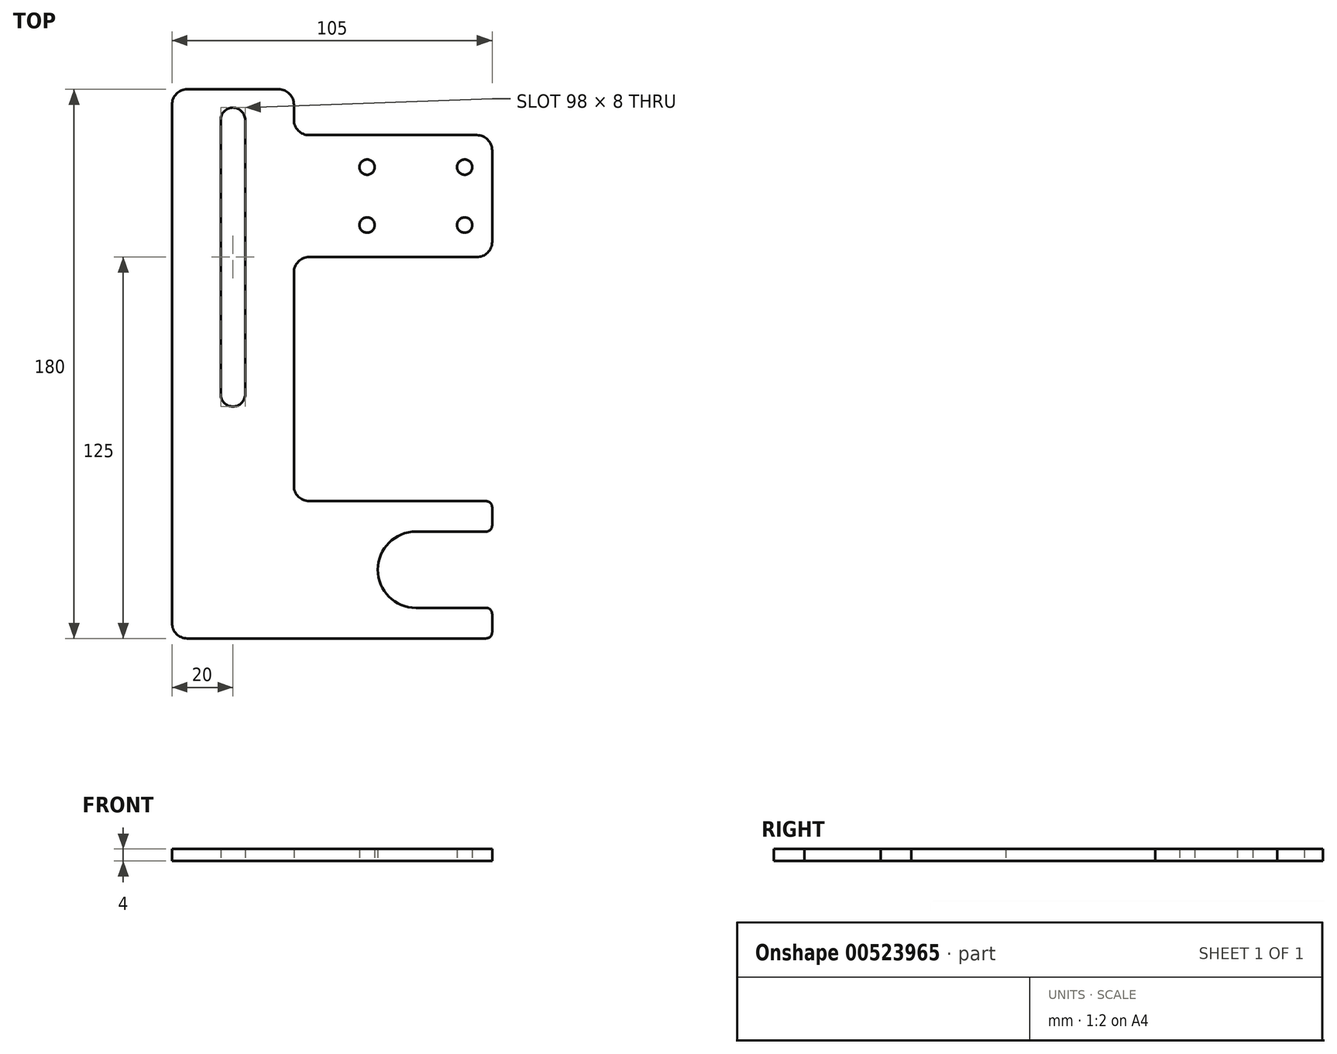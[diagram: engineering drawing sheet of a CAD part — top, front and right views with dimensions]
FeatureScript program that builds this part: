
annotation { "Feature Type Name" : "Feature", "Feature Type Description" : "" }
export const myFeature = defineFeature(function(context is Context, id is Id, definition is map)
    precondition{}
    {
        {
            var Q0;
            Q0=qCreatedBy(makeId("Top.planeOp"),FACE);
            var sketch = newSketch(context, id + "F0", { "sketchPlane" : qUnion([Q0])});
            skArc(sketch, "E0", {"start": v(0, 12.5) * mm, "mid": v(-12.5, 0) * mm, "end": v(0, -12.5) * mm});
            skLineSegment(sketch, "E1", {"start": v(0, 0) * mm, "end": v(-80, 0) * mm, "construction": true});
            skLineSegment(sketch, "E2.top", {"start": v(-75, -22.5) * mm, "end": v(23, -22.5) * mm});
            skLineSegment(sketch, "E2.right", {"start": v(25, 20.5) * mm, "end": v(25, 14.5) * mm});
            skLineSegment(sketch, "E3", {"start": v(23, 12.5) * mm, "end": v(0, 12.5) * mm});
            skLineSegment(sketch, "E4.MirrorCS", {"start": v(23, -12.5) * mm, "end": v(0, -12.5) * mm});
            skLineSegment(sketch, "E5.trimOffspring", {"start": v(25, -14.5) * mm, "end": v(25, -20.5) * mm});
            skPoint(sketch, "E6.visualSharp", {"position": v(25, -12.5) * mm});
            skArc(sketch, "E6.filletArc", {"start": v(25, -14.5) * mm, "mid": v(24.41, -13.09) * mm, "end": v(23, -12.5) * mm});
            skPoint(sketch, "E7.visualSharp", {"position": v(25, 12.5) * mm});
            skArc(sketch, "E7.filletArc", {"start": v(23, 12.5) * mm, "mid": v(24.41, 13.09) * mm, "end": v(25, 14.5) * mm});
            skPoint(sketch, "E8.visualSharp", {"position": v(25, 22.5) * mm});
            skArc(sketch, "E8.filletArc", {"start": v(25, 20.5) * mm, "mid": v(24.41, 21.91) * mm, "end": v(23, 22.5) * mm});
            skPoint(sketch, "E9.visualSharp", {"position": v(25, -22.5) * mm});
            skArc(sketch, "E9.filletArc", {"start": v(23, -22.5) * mm, "mid": v(24.41, -21.91) * mm, "end": v(25, -20.5) * mm});
            skPoint(sketch, "E10", {"position": v(-72, 15) * mm});
            skPoint(sketch, "E11", {"position": v(-57, 15) * mm});
            skPoint(sketch, "E12.MirrorP", {"position": v(-72, -15) * mm});
            skPoint(sketch, "E13.MirrorP", {"position": v(-57, -15) * mm});
            skLineSegment(sketch, "E14.top", {"start": v(-45, 157.5) * mm, "end": v(-75, 157.5) * mm});
            skLineSegment(sketch, "E14.left", {"start": v(-40, 27.5) * mm, "end": v(-40, 97.5) * mm});
            skLineSegment(sketch, "E14.right", {"start": v(-80, -17.5) * mm, "end": v(-80, 152.5) * mm});
            skLineSegment(sketch, "E15.trimOffspring", {"start": v(-35, 22.5) * mm, "end": v(23, 22.5) * mm});
            skPoint(sketch, "E16.visualSharp", {"position": v(-40, 22.5) * mm});
            skArc(sketch, "E16.filletArc", {"start": v(-40, 27.5) * mm, "mid": v(-38.54, 23.96) * mm, "end": v(-35, 22.5) * mm});
            skPoint(sketch, "E17.visualSharp", {"position": v(-80, -22.5) * mm});
            skArc(sketch, "E17.filletArc", {"start": v(-80, -17.5) * mm, "mid": v(-78.54, -21.04) * mm, "end": v(-75, -22.5) * mm});
            skLineSegment(sketch, "E18", {"start": v(-60, 147.5) * mm, "end": v(-60, 57.5) * mm, "construction": true});
            skPoint(sketch, "E19.orphan", {"position": v(-60, 157.5) * mm});
            skArc(sketch, "E20.0.startCap", {"start": v(-64, 147.5) * mm, "mid": v(-60, 151.5) * mm, "end": v(-56, 147.5) * mm});
            skArc(sketch, "E20.0.endCap", {"start": v(-56, 57.5) * mm, "mid": v(-60, 53.5) * mm, "end": v(-64, 57.5) * mm});
            skLineSegment(sketch, "E20.0.left", {"start": v(-56, 147.5) * mm, "end": v(-56, 57.5) * mm});
            skLineSegment(sketch, "E20.0.right", {"start": v(-64, 147.5) * mm, "end": v(-64, 57.5) * mm});
            skPoint(sketch, "E21.visualSharp", {"position": v(-80, 157.5) * mm});
            skArc(sketch, "E21.filletArc", {"start": v(-75, 157.5) * mm, "mid": v(-78.54, 156.04) * mm, "end": v(-80, 152.5) * mm});
            skPoint(sketch, "E22.visualSharp", {"position": v(-40, 157.5) * mm});
            skArc(sketch, "E22.filletArc", {"start": v(-40, 152.5) * mm, "mid": v(-41.46, 156.04) * mm, "end": v(-45, 157.5) * mm});
            skLineSegment(sketch, "E23.bottom", {"start": v(-35, 142.5) * mm, "end": v(20, 142.5) * mm});
            skLineSegment(sketch, "E23.top", {"start": v(-35, 102.5) * mm, "end": v(20, 102.5) * mm});
            skLineSegment(sketch, "E23.right", {"start": v(25, 137.5) * mm, "end": v(25, 107.5) * mm});
            skLineSegment(sketch, "E24.trimOffspring", {"start": v(-40, 147.5) * mm, "end": v(-40, 152.5) * mm});
            skPoint(sketch, "E25.visualSharp", {"position": v(-40, 142.5) * mm});
            skArc(sketch, "E25.filletArc", {"start": v(-40, 147.5) * mm, "mid": v(-38.54, 143.96) * mm, "end": v(-35, 142.5) * mm});
            skPoint(sketch, "E26.visualSharp", {"position": v(-40, 102.5) * mm});
            skArc(sketch, "E26.filletArc", {"start": v(-35, 102.5) * mm, "mid": v(-38.54, 101.04) * mm, "end": v(-40, 97.5) * mm});
            skPoint(sketch, "E27.visualSharp", {"position": v(25, 102.5) * mm});
            skArc(sketch, "E27.filletArc", {"start": v(20, 102.5) * mm, "mid": v(23.54, 103.96) * mm, "end": v(25, 107.5) * mm});
            skPoint(sketch, "E28.visualSharp", {"position": v(25, 142.5) * mm});
            skArc(sketch, "E28.filletArc", {"start": v(25, 137.5) * mm, "mid": v(23.54, 141.04) * mm, "end": v(20, 142.5) * mm});
            skLineSegment(sketch, "E29", {"start": v(0, 14.76) * mm, "end": v(0, 172.75) * mm, "construction": true});
            skLineSegment(sketch, "E30", {"start": v(25, 122.5) * mm, "end": v(-21.32, 122.5) * mm, "construction": true});
            skPoint(sketch, "E31", {"position": v(-16, 132) * mm});
            skPoint(sketch, "E32", {"position": v(16, 132) * mm});
            skPoint(sketch, "E33.MirrorP", {"position": v(-16, 113) * mm});
            skPoint(sketch, "E34.MirrorP", {"position": v(16, 113) * mm});
            skSolve(sketch);
        }
        {
            var Q0;
            Q0=makeQuery(id+"F0.imprint","IMPRINT",FACE,{"disambiguationData":[TD([[makeQuery(id+"F0.imprint","IMPRINT",EDGE,{"derivedFrom":sQuery(id+"F0.wireOp",EDGE,"E0")}),-1.0]])]});
            extrude(context, id + "F1", {"entities" : qUnion([Q0]), "depth" : 4 * mm, "offsetDistance" : 25 * mm});
        }
        {
            var Q0;
            Q0=sQuery(id+"F0.wireOp",VERTEX,"E31");
            var Q1;
            Q1=sQuery(id+"F0.wireOp",VERTEX,"E32");
            var Q2;
            Q2=sQuery(id+"F0.wireOp",VERTEX,"E34.MirrorP");
            var Q3;
            Q3=sQuery(id+"F0.wireOp",VERTEX,"E33.MirrorP");
            var Q4;
            Q4=makeQuery(id+"F1.opExtrude","SWEPT_BODY",BODY,{"disambiguationData":[OSD([sQuery(id+"F0.wireOp",EDGE,"E0"),sQuery(id+"F0.wireOp",EDGE,"E2.bottom"),sQuery(id+"F0.wireOp",EDGE,"E2.top"),sQuery(id+"F0.wireOp",EDGE,"E2.left"),sQuery(id+"F0.wireOp",EDGE,"E2.right"),sQuery(id+"F0.wireOp",EDGE,"E3"),sQuery(id+"F0.wireOp",EDGE,"E4.MirrorCS"),sQuery(id+"F0.wireOp",EDGE,"E5.trimOffspring"),sQuery(id+"F0.wireOp",EDGE,"E6.filletArc"),sQuery(id+"F0.wireOp",EDGE,"E7.filletArc"),sQuery(id+"F0.wireOp",EDGE,"E8.filletArc"),sQuery(id+"F0.wireOp",EDGE,"E9.filletArc"),sQuery(id+"F0.wireOp",EDGE,"E14.top"),sQuery(id+"F0.wireOp",EDGE,"E14.left"),sQuery(id+"F0.wireOp",EDGE,"E14.right"),sQuery(id+"F0.wireOp",EDGE,"E15.trimOffspring"),sQuery(id+"F0.wireOp",EDGE,"E16.filletArc"),sQuery(id+"F0.wireOp",EDGE,"E17.filletArc"),sQuery(id+"F0.wireOp",EDGE,"E20.0.startCap"),sQuery(id+"F0.wireOp",EDGE,"E20.0.endCap"),sQuery(id+"F0.wireOp",EDGE,"E20.0.left"),sQuery(id+"F0.wireOp",EDGE,"E20.0.right"),sQuery(id+"F0.wireOp",EDGE,"E21.filletArc"),sQuery(id+"F0.wireOp",EDGE,"E22.filletArc"),sQuery(id+"F0.wireOp",EDGE,"E23.bottom"),sQuery(id+"F0.wireOp",EDGE,"E23.top"),sQuery(id+"F0.wireOp",EDGE,"E23.right"),sQuery(id+"F0.wireOp",EDGE,"E24.trimOffspring"),sQuery(id+"F0.wireOp",EDGE,"E25.filletArc"),sQuery(id+"F0.wireOp",EDGE,"E26.filletArc"),sQuery(id+"F0.wireOp",EDGE,"E27.filletArc"),sQuery(id+"F0.wireOp",EDGE,"E28.filletArc")])]});
            hole(context, id + "F2", {"style" : HoleStyle.SIMPLE, "endStyle" : HoleEndStyle.THROUGH, "oppositeDirection" : true, "standardTappedOrClearance" : lookupTablePath({ "standard" : "ISO", "engagement" : "75%", "pitch" : "1 mm", "size" : "M6", "type" : "Tapped" }), "standardBlindInLast" : lookupTablePath({ "standard" : "ISO", "engagement" : "75%", "pitch" : "1 mm", "size" : "M6", "type" : "Tapped" }), "holeDiameter" : 5 * mm, "showTappedDepth" : true, "isTappedThrough" : true, "tappedDepth" : 12 * mm, "tapClearance" : 3, "locations" : qUnion([Q0, Q1, Q2, Q3]), "scope" : qUnion([Q4]), "majorDiameter" : 6 * mm});
        }
    });
